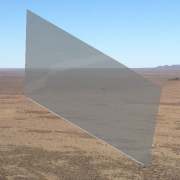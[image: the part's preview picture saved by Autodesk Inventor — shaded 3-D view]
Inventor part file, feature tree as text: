
AUTODESK INVENTOR PART (.ipt)
format: ipt  version: 2013 SP2 (Build 170200200, 200)  size: 152,064 bytes
history: native  units: in
note: dims shown in document units (in); Inventor stores cm internally (conversion verified against a paired STEP export)
features: extrude x4, sketch x4, plane x1
ambient origin geometry x8: Origin, YZ Plane, XZ Plane, XY Plane, X Axis, Y Axis, Z Axis, Center Point
bodies: Solid1 (feature_tree)
feature tree (9):
  extrude  "bottomMateSurface"  Depth=1.0in
  plane  "Work Plane1"
  extrude  "centralPanelPortion"  Depth=0.0481in
  extrude  "extensionRight"  Depth=0.25in
  extrude  "extensionLeft"  Depth=4.0in
  sketch  "Sketch1"  dims[d0=136.0in d1=1.0in]
  sketch  "Sketch2"  dims[d2=0.25in d3=0.0in d4=0.0481in]
  sketch  "Sketch5"  dims[d5=136.0in d6=0.25in]
  sketch  "Sketch6"  dims[d7=80.0in d8=0.0in d16=4.0in d17=11.0in d18=0.25in d19=0.0in d20=4.0in d21=11.0in d22=0.25in d23=0.0in]
